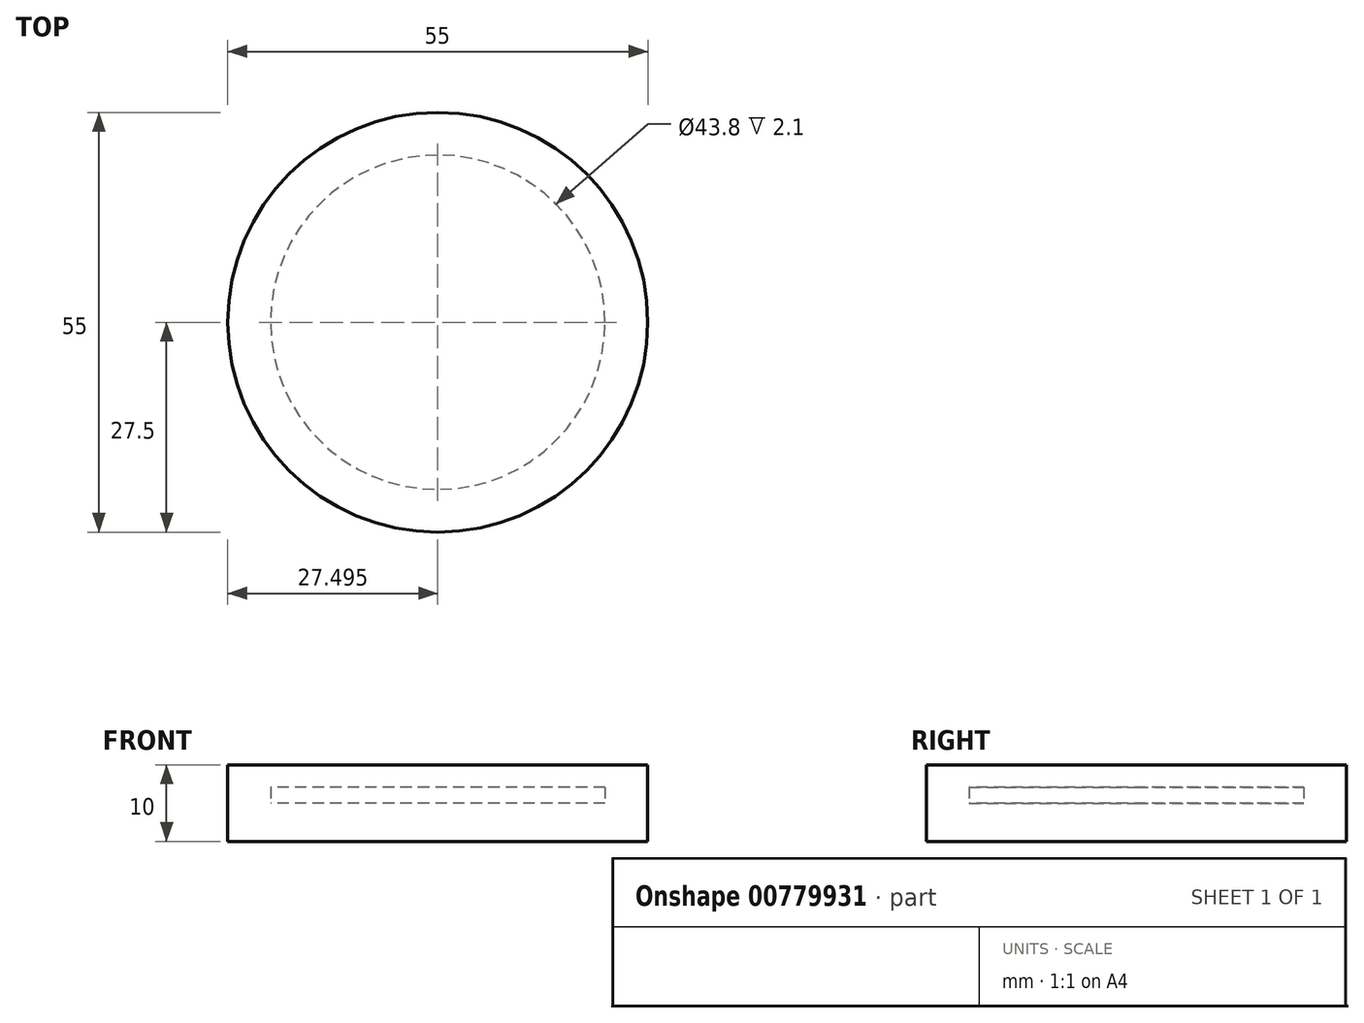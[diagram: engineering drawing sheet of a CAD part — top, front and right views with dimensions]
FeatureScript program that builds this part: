
annotation { "Feature Type Name" : "Feature", "Feature Type Description" : "" }
export const myFeature = defineFeature(function(context is Context, id is Id, definition is map)
    precondition{}
    {
        {
            var Q0;
            Q0=qCreatedBy(makeId("Top.planeOp"),FACE);
            var sketch = newSketch(context, id + "F0", { "sketchPlane" : qUnion([Q0])});
            skCircle(sketch, "E0", {"center": v(-37.64, 39.46) * mm, "radius": 27.5 * mm});
            skSolve(sketch);
        }
        {
            var Q0;
            Q0 = qSketchRegion(id + "F0", true);
            extrude(context, id + "F1", {"entities" : qUnion([Q0]), "depth" : 5 * mm, "offsetDistance" : 25 * mm, "hasSecondDirection" : true, "secondDirectionOppositeDirection" : true, "secondDirectionDepth" : 5 * mm});
        }
        {
            var Q0;
            Q0=makeQuery(id+"F1.opExtrude","CAP_FACE",FACE,{"disambiguationData":[OSD([sQuery(id+"F0.wireOp",EDGE,"E0")])],"isStart":false});
            var sketch = newSketch(context, id + "F2", { "sketchPlane" : qUnion([Q0])});
            skSolve(sketch);
        }
        {
            var Q0;
            Q0=qCreatedBy(makeId("Top.planeOp"),FACE);
            var sketch = newSketch(context, id + "F3", { "sketchPlane" : qUnion([Q0])});
            skCircle(sketch, "E1.0", {"center": v(-37.64, 39.46) * mm, "radius": 21.9 * mm});
            skSolve(sketch);
        }
        {
            var Q0;
            Q0 = qSketchRegion(id + "F3", true);
            extrude(context, id + "F4", {"entities" : qUnion([Q0]), "operationType" : NewBodyOperationType.REMOVE, "depth" : 2.1 * mm, "offsetDistance" : 25 * mm});
        }
    });
